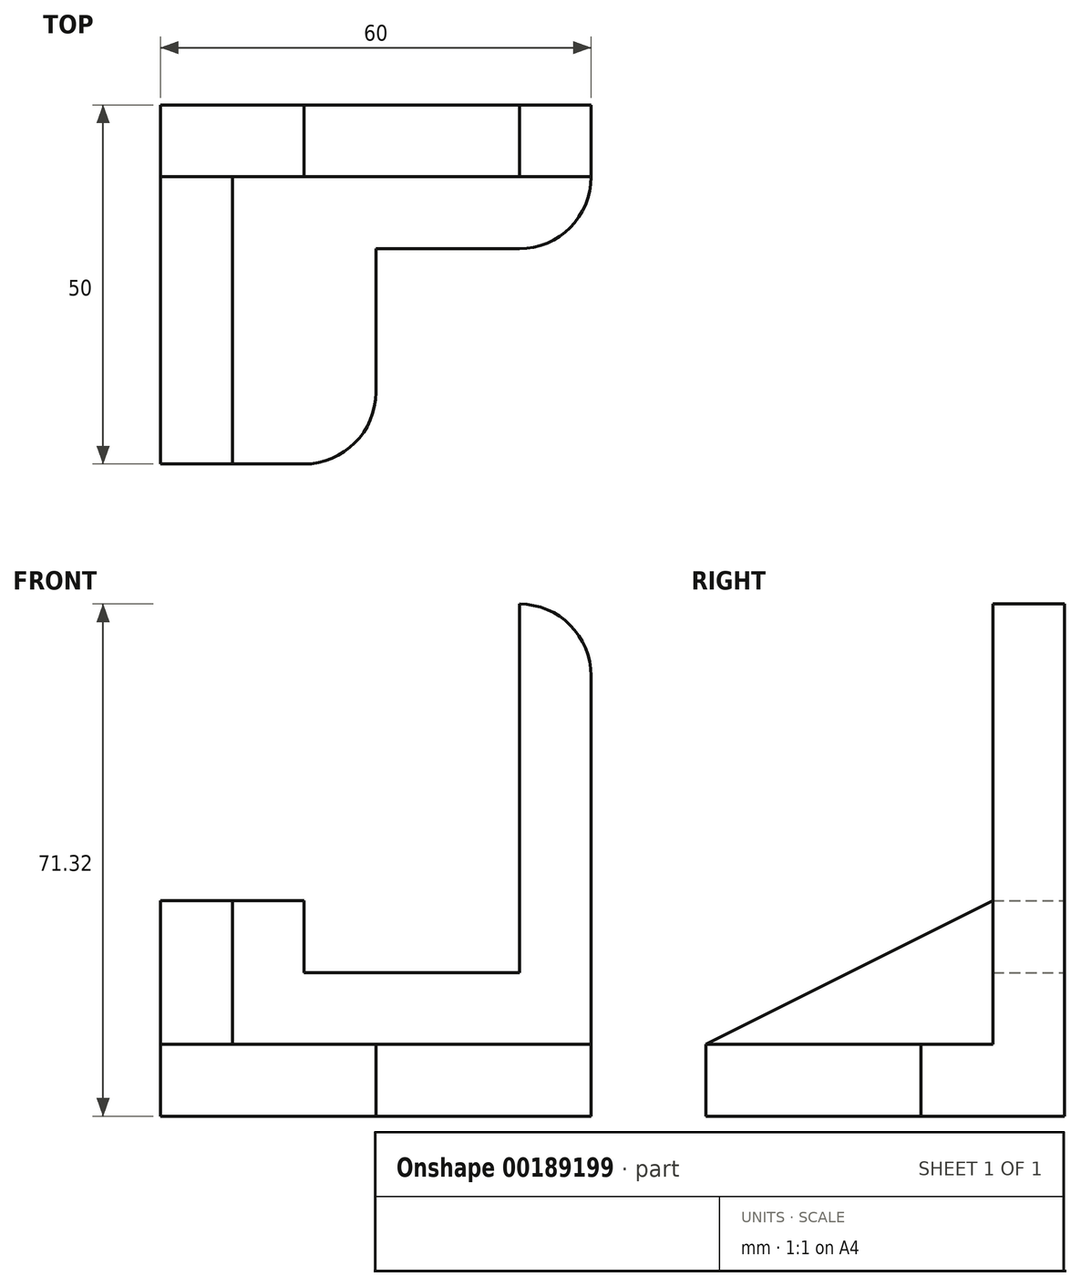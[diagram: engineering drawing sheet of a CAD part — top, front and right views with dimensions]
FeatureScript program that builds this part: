
annotation { "Feature Type Name" : "Feature", "Feature Type Description" : "" }
export const myFeature = defineFeature(function(context is Context, id is Id, definition is map)
    precondition{}
    {
        {
            var Q0;
            Q0=qCreatedBy(makeId("Top.planeOp"),FACE);
            var sketch = newSketch(context, id + "F0", { "sketchPlane" : qUnion([Q0])});
            skLineSegment(sketch, "E0", {"start": v(0, 0) * mm, "end": v(60, 0) * mm});
            skLineSegment(sketch, "E1", {"start": v(60, 0) * mm, "end": v(60, -10) * mm});
            skLineSegment(sketch, "E2", {"start": v(50, -20) * mm, "end": v(30, -20) * mm});
            skLineSegment(sketch, "E3", {"start": v(30, -20) * mm, "end": v(30, -40) * mm});
            skLineSegment(sketch, "E4", {"start": v(20, -50) * mm, "end": v(0, -50) * mm});
            skLineSegment(sketch, "E5", {"start": v(0, -50) * mm, "end": v(0, 0) * mm});
            skPoint(sketch, "E6.visualSharp", {"position": v(30, -50) * mm});
            skArc(sketch, "E6.filletArc", {"start": v(20, -50) * mm, "mid": v(27.07, -47.07) * mm, "end": v(30, -40) * mm});
            skPoint(sketch, "E7.visualSharp", {"position": v(60, -20) * mm});
            skArc(sketch, "E7.filletArc", {"start": v(50, -20) * mm, "mid": v(57.07, -17.07) * mm, "end": v(60, -10) * mm});
            skSolve(sketch);
        }
        {
            var Q0;
            Q0=makeQuery(id+"F0.imprint","IMPRINT",FACE,{"disambiguationData":[TD([[makeQuery(id+"F0.imprint","IMPRINT",EDGE,{"derivedFrom":sQuery(id+"F0.wireOp",EDGE,"E0")}),-1.0]])]});
            extrude(context, id + "F1", {"entities" : qUnion([Q0]), "depth" : 10 * mm});
        }
        {
            var Q0;
            Q0=qCreatedBy(makeId("Front.planeOp"),FACE);
            var sketch = newSketch(context, id + "F2", { "sketchPlane" : qUnion([Q0])});
            skLineSegment(sketch, "E8", {"start": v(0, 10) * mm, "end": v(0, 30) * mm});
            skLineSegment(sketch, "E9", {"start": v(0, 30) * mm, "end": v(20, 30) * mm});
            skLineSegment(sketch, "E10", {"start": v(20, 30) * mm, "end": v(20, 20) * mm});
            skLineSegment(sketch, "E11", {"start": v(20, 20) * mm, "end": v(50, 20) * mm});
            skLineSegment(sketch, "E12", {"start": v(50, 20) * mm, "end": v(50, 71.32) * mm});
            skLineSegment(sketch, "E13", {"start": v(50, 71.32) * mm, "end": v(50, 71.32) * mm});
            skLineSegment(sketch, "E14", {"start": v(60, 61.32) * mm, "end": v(60, 10) * mm});
            skPoint(sketch, "E15.visualSharp", {"position": v(60, 71.32) * mm});
            skArc(sketch, "E15.filletArc", {"start": v(60, 61.32) * mm, "mid": v(57.07, 68.4) * mm, "end": v(50, 71.32) * mm});
            skLineSegment(sketch, "E16", {"start": v(0, 10) * mm, "end": v(60, 10) * mm});
            skSolve(sketch);
        }
        {
            var Q0;
            Q0 = qSketchRegion(id + "F2", true);
            extrude(context, id + "F3", {"entities" : qUnion([Q0]), "operationType" : NewBodyOperationType.ADD, "depth" : 10 * mm});
        }
        {
            var Q0;
            Q0=qCreatedBy(makeId("Right.planeOp"),FACE);
            var sketch = newSketch(context, id + "F4", { "sketchPlane" : qUnion([Q0])});
            skLineSegment(sketch, "E17.0", {"start": v(-10, 10) * mm, "end": v(-10, 30) * mm});
            skLineSegment(sketch, "E18.0", {"start": v(-50, 10) * mm, "end": v(-10, 10) * mm});
            skLineSegment(sketch, "E19", {"start": v(-10, 30) * mm, "end": v(-50, 10) * mm});
            skSolve(sketch);
        }
        {
            var Q0;
            Q0=makeQuery(id+"F4.imprint","IMPRINT",FACE,{"disambiguationData":[TD([[makeQuery(id+"F4.imprint","IMPRINT",EDGE,{"derivedFrom":sQuery(id+"F4.wireOp",EDGE,"E17.0")}),1.0]])]});
            extrude(context, id + "F5", {"entities" : qUnion([Q0]), "operationType" : NewBodyOperationType.ADD, "depth" : 10 * mm});
        }
    });
